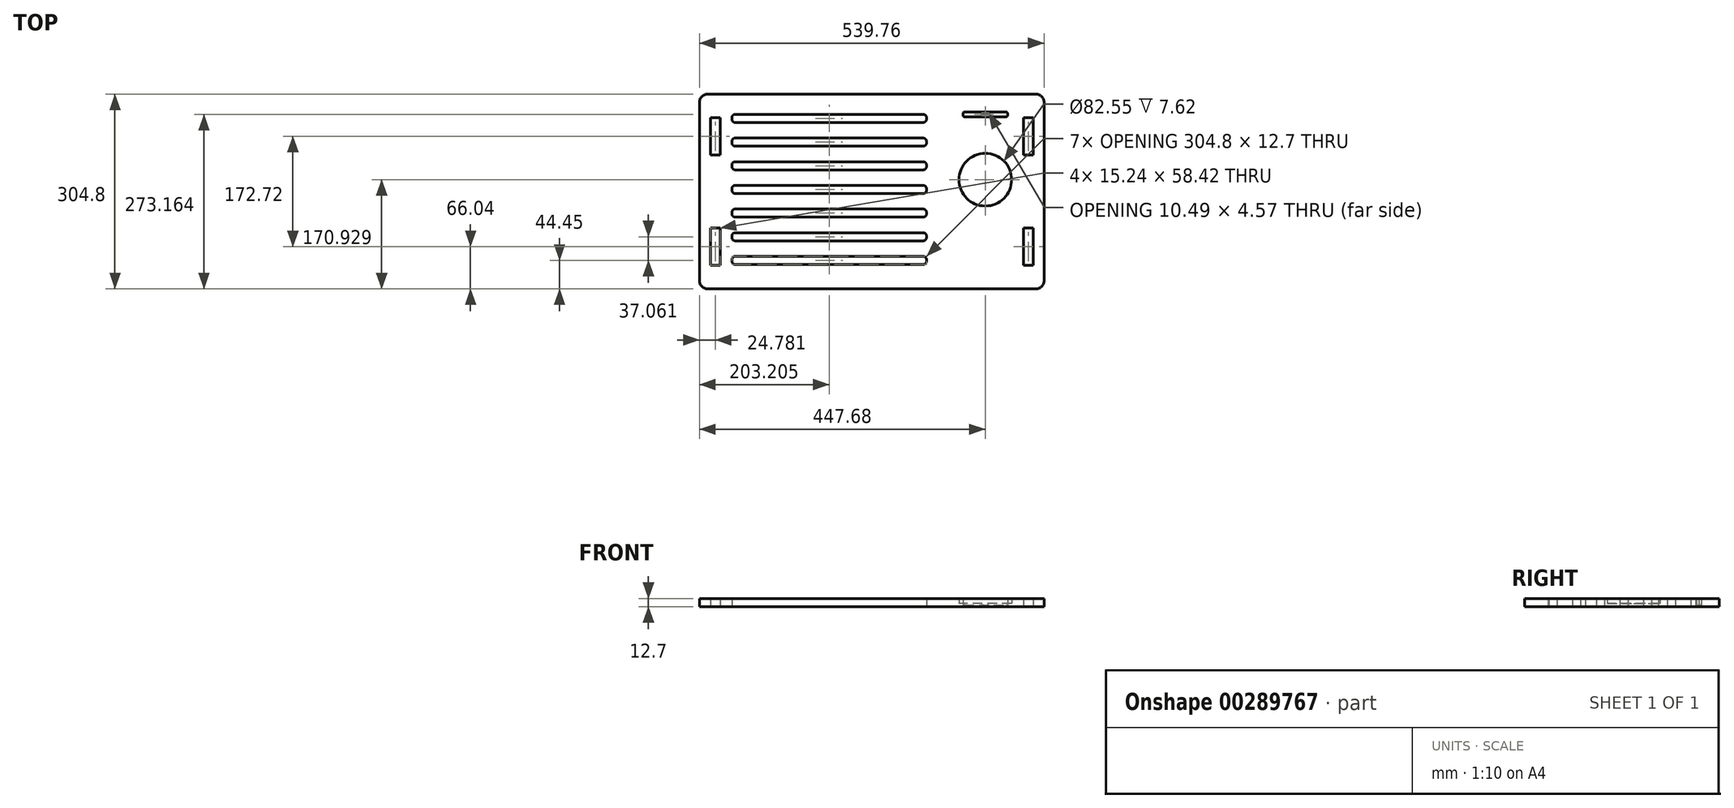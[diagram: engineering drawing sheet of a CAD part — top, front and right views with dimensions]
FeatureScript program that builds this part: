
annotation { "Feature Type Name" : "Feature", "Feature Type Description" : "" }
export const myFeature = defineFeature(function(context is Context, id is Id, definition is map)
    precondition{}
    {
        {
            var Q0;
            Q0=qCreatedBy(makeId("Top.planeOp"),FACE);
            var sketch = newSketch(context, id + "F0", { "sketchPlane" : qUnion([Q0])});
            skLineSegment(sketch, "E0.bottom", {"start": v(269.88, 152.4) * mm, "end": v(-269.88, 152.4) * mm});
            skLineSegment(sketch, "E0.top", {"start": v(269.88, -152.4) * mm, "end": v(-269.88, -152.4) * mm});
            skLineSegment(sketch, "E0.left", {"start": v(269.88, 152.4) * mm, "end": v(269.88, -152.4) * mm});
            skLineSegment(sketch, "E0.right", {"start": v(-269.88, 152.4) * mm, "end": v(-269.88, -152.4) * mm});
            skPoint(sketch, "E0.middle", {"position": v(0, 0) * mm});
            skLineSegment(sketch, "E1.bottom", {"start": v(-219.08, 120.76) * mm, "end": v(85.72, 120.76) * mm});
            skLineSegment(sketch, "E1.top", {"start": v(-219.08, 108.06) * mm, "end": v(85.72, 108.06) * mm});
            skLineSegment(sketch, "E1.left", {"start": v(-219.08, 120.76) * mm, "end": v(-219.08, 108.06) * mm});
            skLineSegment(sketch, "E1.right", {"start": v(85.72, 120.76) * mm, "end": v(85.72, 108.06) * mm});
            skLineSegment(sketch, "E2.bottom", {"start": v(-219.08, 83.7) * mm, "end": v(85.72, 83.7) * mm});
            skLineSegment(sketch, "E2.top", {"start": v(-219.08, 71) * mm, "end": v(85.72, 71) * mm});
            skLineSegment(sketch, "E2.left", {"start": v(-219.08, 83.7) * mm, "end": v(-219.08, 71) * mm});
            skLineSegment(sketch, "E2.right", {"start": v(85.72, 83.7) * mm, "end": v(85.72, 71) * mm});
            skLineSegment(sketch, "E3.bottom", {"start": v(-219.08, -64.54) * mm, "end": v(85.72, -64.54) * mm});
            skLineSegment(sketch, "E3.top", {"start": v(-219.08, -77.24) * mm, "end": v(85.72, -77.24) * mm});
            skLineSegment(sketch, "E3.left", {"start": v(-219.08, -64.54) * mm, "end": v(-219.08, -77.24) * mm});
            skLineSegment(sketch, "E3.right", {"start": v(85.72, -64.54) * mm, "end": v(85.72, -77.24) * mm});
            skLineSegment(sketch, "E4.bottom", {"start": v(-219.08, 9.58) * mm, "end": v(85.72, 9.58) * mm});
            skLineSegment(sketch, "E4.top", {"start": v(-219.08, -3.12) * mm, "end": v(85.72, -3.12) * mm});
            skLineSegment(sketch, "E4.left", {"start": v(-219.08, 9.58) * mm, "end": v(-219.08, -3.12) * mm});
            skLineSegment(sketch, "E4.right", {"start": v(85.72, 9.58) * mm, "end": v(85.72, -3.12) * mm});
            skLineSegment(sketch, "E5.bottom", {"start": v(-219.08, -27.48) * mm, "end": v(85.72, -27.48) * mm});
            skLineSegment(sketch, "E5.top", {"start": v(-219.08, -40.18) * mm, "end": v(85.72, -40.18) * mm});
            skLineSegment(sketch, "E5.left", {"start": v(-219.08, -27.48) * mm, "end": v(-219.08, -40.18) * mm});
            skLineSegment(sketch, "E5.right", {"start": v(85.72, -27.48) * mm, "end": v(85.72, -40.18) * mm});
            skLineSegment(sketch, "E6.bottom", {"start": v(-219.08, 46.64) * mm, "end": v(85.72, 46.64) * mm});
            skLineSegment(sketch, "E6.top", {"start": v(-219.08, 33.94) * mm, "end": v(85.72, 33.94) * mm});
            skLineSegment(sketch, "E6.left", {"start": v(-219.08, 46.64) * mm, "end": v(-219.08, 33.94) * mm});
            skLineSegment(sketch, "E6.right", {"start": v(85.72, 46.64) * mm, "end": v(85.72, 33.94) * mm});
            skLineSegment(sketch, "E7.bottom", {"start": v(-219.08, -101.6) * mm, "end": v(85.72, -101.6) * mm});
            skLineSegment(sketch, "E7.top", {"start": v(-219.08, -114.3) * mm, "end": v(85.72, -114.3) * mm});
            skLineSegment(sketch, "E7.left", {"start": v(-219.08, -101.6) * mm, "end": v(-219.08, -114.3) * mm});
            skLineSegment(sketch, "E7.right", {"start": v(85.72, -101.6) * mm, "end": v(85.72, -114.3) * mm});
            skLineSegment(sketch, "E8", {"start": v(-219.08, 152.4) * mm, "end": v(-219.07, -152.4) * mm, "construction": true});
            skLineSegment(sketch, "E9", {"start": v(-146.4, 71) * mm, "end": v(-146.4, 46.64) * mm, "construction": true});
            skLineSegment(sketch, "E10", {"start": v(-146.45, 108.06) * mm, "end": v(-146.45, 83.7) * mm, "construction": true});
            skLineSegment(sketch, "E11", {"start": v(-146.4, 33.94) * mm, "end": v(-146.4, 9.58) * mm, "construction": true});
            skLineSegment(sketch, "E12", {"start": v(-147.4, -3.12) * mm, "end": v(-147.4, -27.48) * mm, "construction": true});
            skLineSegment(sketch, "E13", {"start": v(-151.42, -40.18) * mm, "end": v(-151.42, -64.54) * mm, "construction": true});
            skLineSegment(sketch, "E14", {"start": v(-148.27, -77.24) * mm, "end": v(-148.27, -101.6) * mm, "construction": true});
            skLineSegment(sketch, "E15", {"start": v(-269.88, 120.76) * mm, "end": v(269.88, 120.76) * mm, "construction": true});
            skLineSegment(sketch, "E16", {"start": v(-269.88, -114.3) * mm, "end": v(269.88, -114.3) * mm, "construction": true});
            skLineSegment(sketch, "E17", {"start": v(-36.06, 137.03) * mm, "end": v(-36.06, 111.63) * mm, "construction": true});
            skLineSegment(sketch, "E18.bottom", {"start": v(142.87, 124.57) * mm, "end": v(212.72, 124.57) * mm});
            skLineSegment(sketch, "E18.top", {"start": v(142.87, 116.95) * mm, "end": v(212.72, 116.95) * mm});
            skLineSegment(sketch, "E18.left", {"start": v(142.87, 124.57) * mm, "end": v(142.87, 116.95) * mm});
            skLineSegment(sketch, "E18.right", {"start": v(212.72, 124.57) * mm, "end": v(212.72, 116.95) * mm});
            skLineSegment(sketch, "E19.bottom", {"start": v(172.55, 123.05) * mm, "end": v(183.05, 123.05) * mm});
            skLineSegment(sketch, "E19.top", {"start": v(172.55, 118.48) * mm, "end": v(183.05, 118.48) * mm});
            skLineSegment(sketch, "E19.left", {"start": v(172.55, 123.05) * mm, "end": v(172.55, 118.48) * mm});
            skLineSegment(sketch, "E19.right", {"start": v(183.05, 123.05) * mm, "end": v(183.05, 118.48) * mm});
            skLineSegment(sketch, "E20", {"start": v(142.87, 120.76) * mm, "end": v(212.72, 120.76) * mm, "construction": true});
            skLineSegment(sketch, "E21", {"start": v(177.8, 116.95) * mm, "end": v(177.8, 124.57) * mm, "construction": true});
            skLineSegment(sketch, "E22", {"start": v(172.55, 120.76) * mm, "end": v(183.05, 120.76) * mm, "construction": true});
            skLineSegment(sketch, "E23", {"start": v(177.8, 118.48) * mm, "end": v(177.8, 123.05) * mm, "construction": true});
            skCircle(sketch, "E24", {"center": v(177.8, 18.53) * mm, "radius": 47.63 * mm});
            skCircle(sketch, "E25", {"center": v(177.8, 18.53) * mm, "radius": 41.28 * mm});
            skLineSegment(sketch, "E26", {"start": v(177.8, 202.35) * mm, "end": v(177.8, -203.89) * mm, "construction": true});
            skLineSegment(sketch, "E27", {"start": v(-245.1, 152.4) * mm, "end": v(-245.1, -152.4) * mm, "construction": true});
            skLineSegment(sketch, "E28.bottom", {"start": v(-237.48, 115.57) * mm, "end": v(-252.72, 115.57) * mm});
            skLineSegment(sketch, "E28.top", {"start": v(-237.48, 57.15) * mm, "end": v(-252.72, 57.15) * mm});
            skLineSegment(sketch, "E28.left", {"start": v(-237.48, 115.57) * mm, "end": v(-237.48, 57.15) * mm});
            skLineSegment(sketch, "E28.right", {"start": v(-252.72, 115.57) * mm, "end": v(-252.72, 57.15) * mm});
            skPoint(sketch, "E28.middle", {"position": v(-245.1, 86.36) * mm});
            skLineSegment(sketch, "E29.MirrorCS", {"start": v(237.48, 115.57) * mm, "end": v(252.72, 115.57) * mm});
            skLineSegment(sketch, "E30.MirrorCS", {"start": v(252.72, 115.57) * mm, "end": v(252.72, 57.15) * mm});
            skLineSegment(sketch, "E31.MirrorCS", {"start": v(237.48, 115.57) * mm, "end": v(237.48, 57.15) * mm});
            skLineSegment(sketch, "E32.MirrorCS", {"start": v(237.48, 57.15) * mm, "end": v(252.72, 57.15) * mm});
            skPoint(sketch, "E33.MirrorP", {"position": v(245.1, 86.36) * mm});
            skLineSegment(sketch, "E34.MirrorCS", {"start": v(-237.48, -115.57) * mm, "end": v(-252.72, -115.57) * mm});
            skLineSegment(sketch, "E35.MirrorCS", {"start": v(-237.48, -57.15) * mm, "end": v(-252.72, -57.15) * mm});
            skPoint(sketch, "E36.MirrorP", {"position": v(-245.1, -86.36) * mm});
            skLineSegment(sketch, "E37.MirrorCS", {"start": v(-237.48, -115.57) * mm, "end": v(-237.48, -57.15) * mm});
            skLineSegment(sketch, "E38.MirrorCS", {"start": v(-252.72, -115.57) * mm, "end": v(-252.72, -57.15) * mm});
            skLineSegment(sketch, "E39.MirrorCS", {"start": v(252.72, -115.57) * mm, "end": v(252.72, -57.15) * mm});
            skLineSegment(sketch, "E40.MirrorCS", {"start": v(237.48, -115.57) * mm, "end": v(237.48, -57.15) * mm});
            skLineSegment(sketch, "E41.MirrorCS", {"start": v(237.48, -115.57) * mm, "end": v(252.72, -115.57) * mm});
            skPoint(sketch, "E42.MirrorP", {"position": v(245.1, -86.36) * mm});
            skLineSegment(sketch, "E43.MirrorCS", {"start": v(237.48, -57.15) * mm, "end": v(252.72, -57.15) * mm});
            skLineSegment(sketch, "E44.MirrorCS", {"start": v(269.88, -152.4) * mm, "end": v(269.88, 152.4) * mm});
            skSolve(sketch);
        }
        {
            var Q0;
            Q0=makeQuery(id+"F0.imprint","IMPRINT",FACE,{"disambiguationData":[TD([[makeQuery(id+"F0.imprint","IMPRINT",EDGE,{"derivedFrom":sQuery(id+"F0.wireOp",EDGE,"E0.bottom")}),1.0]])]});
            extrude(context, id + "F1", {"entities" : qUnion([Q0]), "depth" : 12.7 * mm});
        }
        {
            var Q0;
            Q0=makeQuery(id+"F0.imprint","IMPRINT",FACE,{"disambiguationData":[TD([[makeQuery(id+"F0.imprint","IMPRINT",EDGE,{"derivedFrom":sQuery(id+"F0.wireOp",EDGE,"E18.bottom")}),-1.0]])]});
            extrude(context, id + "F2", {"entities" : qUnion([Q0]), "operationType" : NewBodyOperationType.ADD, "depth" : 2.54 * mm});
        }
        {
            var Q0;
            Q0=makeQuery(id+"F0.imprint","IMPRINT",FACE,{"disambiguationData":[TD([[makeQuery(id+"F0.imprint","IMPRINT",EDGE,{"derivedFrom":sQuery(id+"F0.wireOp",EDGE,"E24")}),1.0]])]});
            extrude(context, id + "F3", {"entities" : qUnion([Q0]), "operationType" : NewBodyOperationType.ADD, "depth" : 12.7 * mm});
        }
        {
            var Q0;
            Q0=makeQuery(id+"F0.imprint","IMPRINT",FACE,{"disambiguationData":[TD([[makeQuery(id+"F0.imprint","IMPRINT",EDGE,{"derivedFrom":sQuery(id+"F0.wireOp",EDGE,"E25")}),1.0]])]});
            extrude(context, id + "F4", {"entities" : qUnion([Q0]), "operationType" : NewBodyOperationType.ADD, "depth" : 5.08 * mm});
        }
        {
            var Q0;
            Q0=makeQuery(id+"F1.opExtrude","SWEPT_EDGE",EDGE,{"disambiguationData":[OSD([sQuery(id+"F0.wireOp",EDGE,"E0.bottom"),sQuery(id+"F0.wireOp",EDGE,"E0.right")])]});
            var Q1;
            Q1=makeQuery(id+"F1.opExtrude","SWEPT_EDGE",EDGE,{"disambiguationData":[OSD([sQuery(id+"F0.wireOp",EDGE,"E0.bottom"),sQuery(id+"F0.wireOp",EDGE,"E0.left")])]});
            var Q2;
            Q2=makeQuery(id+"F1.opExtrude","SWEPT_EDGE",EDGE,{"disambiguationData":[OSD([sQuery(id+"F0.wireOp",EDGE,"E0.top"),sQuery(id+"F0.wireOp",EDGE,"E0.left")])]});
            var Q3;
            Q3=makeQuery(id+"F1.opExtrude","SWEPT_EDGE",EDGE,{"disambiguationData":[OSD([sQuery(id+"F0.wireOp",EDGE,"E0.top"),sQuery(id+"F0.wireOp",EDGE,"E0.right")])]});
            fillet(context, id + "F5", {"entities" : qUnion([Q0, Q1, Q2, Q3]), "radius" : 12.7 * mm, "tangentPropagation" : true, "allowEdgeOverflow" : false});
        }
        {
            var Q0;
            Q0=makeQuery(id+"F1.opExtrude","SWEPT_EDGE",EDGE,{"disambiguationData":[OSD([sQuery(id+"F0.wireOp",EDGE,"E1.bottom"),sQuery(id+"F0.wireOp",EDGE,"E1.left")])]});
            var Q1;
            Q1=makeQuery(id+"F1.opExtrude","SWEPT_EDGE",EDGE,{"disambiguationData":[OSD([sQuery(id+"F0.wireOp",EDGE,"E1.bottom"),sQuery(id+"F0.wireOp",EDGE,"E1.right")])]});
            var Q2;
            Q2=makeQuery(id+"F1.opExtrude","SWEPT_EDGE",EDGE,{"disambiguationData":[OSD([sQuery(id+"F0.wireOp",EDGE,"E6.top"),sQuery(id+"F0.wireOp",EDGE,"E6.left")])]});
            var Q3;
            Q3=makeQuery(id+"F1.opExtrude","SWEPT_EDGE",EDGE,{"disambiguationData":[OSD([sQuery(id+"F0.wireOp",EDGE,"E4.top"),sQuery(id+"F0.wireOp",EDGE,"E4.left")])]});
            var Q4;
            Q4=makeQuery(id+"F1.opExtrude","SWEPT_EDGE",EDGE,{"disambiguationData":[OSD([sQuery(id+"F0.wireOp",EDGE,"E5.top"),sQuery(id+"F0.wireOp",EDGE,"E5.left")])]});
            var Q5;
            Q5=makeQuery(id+"F1.opExtrude","SWEPT_EDGE",EDGE,{"disambiguationData":[OSD([sQuery(id+"F0.wireOp",EDGE,"E3.top"),sQuery(id+"F0.wireOp",EDGE,"E3.left")])]});
            var Q6;
            Q6=makeQuery(id+"F1.opExtrude","SWEPT_EDGE",EDGE,{"disambiguationData":[OSD([sQuery(id+"F0.wireOp",EDGE,"E7.top"),sQuery(id+"F0.wireOp",EDGE,"E7.left")])]});
            var Q7;
            Q7=makeQuery(id+"F1.opExtrude","SWEPT_EDGE",EDGE,{"disambiguationData":[OSD([sQuery(id+"F0.wireOp",EDGE,"E1.top"),sQuery(id+"F0.wireOp",EDGE,"E1.left")])]});
            var Q8;
            Q8=makeQuery(id+"F1.opExtrude","SWEPT_EDGE",EDGE,{"disambiguationData":[OSD([sQuery(id+"F0.wireOp",EDGE,"E2.top"),sQuery(id+"F0.wireOp",EDGE,"E2.left")])]});
            var Q9;
            Q9=makeQuery(id+"F1.opExtrude","SWEPT_EDGE",EDGE,{"disambiguationData":[OSD([sQuery(id+"F0.wireOp",EDGE,"E1.top"),sQuery(id+"F0.wireOp",EDGE,"E1.right")])]});
            var Q10;
            Q10=makeQuery(id+"F1.opExtrude","SWEPT_EDGE",EDGE,{"disambiguationData":[OSD([sQuery(id+"F0.wireOp",EDGE,"E2.top"),sQuery(id+"F0.wireOp",EDGE,"E2.right")])]});
            var Q11;
            Q11=makeQuery(id+"F1.opExtrude","SWEPT_EDGE",EDGE,{"disambiguationData":[OSD([sQuery(id+"F0.wireOp",EDGE,"E6.top"),sQuery(id+"F0.wireOp",EDGE,"E6.right")])]});
            var Q12;
            Q12=makeQuery(id+"F1.opExtrude","SWEPT_EDGE",EDGE,{"disambiguationData":[OSD([sQuery(id+"F0.wireOp",EDGE,"E4.top"),sQuery(id+"F0.wireOp",EDGE,"E4.right")])]});
            var Q13;
            Q13=makeQuery(id+"F1.opExtrude","SWEPT_EDGE",EDGE,{"disambiguationData":[OSD([sQuery(id+"F0.wireOp",EDGE,"E5.top"),sQuery(id+"F0.wireOp",EDGE,"E5.right")])]});
            var Q14;
            Q14=makeQuery(id+"F1.opExtrude","SWEPT_EDGE",EDGE,{"disambiguationData":[OSD([sQuery(id+"F0.wireOp",EDGE,"E3.top"),sQuery(id+"F0.wireOp",EDGE,"E3.right")])]});
            var Q15;
            Q15=makeQuery(id+"F1.opExtrude","SWEPT_EDGE",EDGE,{"disambiguationData":[OSD([sQuery(id+"F0.wireOp",EDGE,"E7.top"),sQuery(id+"F0.wireOp",EDGE,"E7.right")])]});
            var Q16;
            Q16=makeQuery(id+"F1.opExtrude","SWEPT_EDGE",EDGE,{"disambiguationData":[OSD([sQuery(id+"F0.wireOp",EDGE,"E7.bottom"),sQuery(id+"F0.wireOp",EDGE,"E7.right")])]});
            var Q17;
            Q17=makeQuery(id+"F1.opExtrude","SWEPT_EDGE",EDGE,{"disambiguationData":[OSD([sQuery(id+"F0.wireOp",EDGE,"E3.bottom"),sQuery(id+"F0.wireOp",EDGE,"E3.right")])]});
            var Q18;
            Q18=makeQuery(id+"F1.opExtrude","SWEPT_EDGE",EDGE,{"disambiguationData":[OSD([sQuery(id+"F0.wireOp",EDGE,"E5.bottom"),sQuery(id+"F0.wireOp",EDGE,"E5.right")])]});
            var Q19;
            Q19=makeQuery(id+"F1.opExtrude","SWEPT_EDGE",EDGE,{"disambiguationData":[OSD([sQuery(id+"F0.wireOp",EDGE,"E4.bottom"),sQuery(id+"F0.wireOp",EDGE,"E4.right")])]});
            var Q20;
            Q20=makeQuery(id+"F1.opExtrude","SWEPT_EDGE",EDGE,{"disambiguationData":[OSD([sQuery(id+"F0.wireOp",EDGE,"E6.bottom"),sQuery(id+"F0.wireOp",EDGE,"E6.right")])]});
            var Q21;
            Q21=makeQuery(id+"F1.opExtrude","SWEPT_EDGE",EDGE,{"disambiguationData":[OSD([sQuery(id+"F0.wireOp",EDGE,"E2.bottom"),sQuery(id+"F0.wireOp",EDGE,"E2.right")])]});
            var Q22;
            Q22=makeQuery(id+"F1.opExtrude","SWEPT_EDGE",EDGE,{"disambiguationData":[OSD([sQuery(id+"F0.wireOp",EDGE,"E7.bottom"),sQuery(id+"F0.wireOp",EDGE,"E7.left")])]});
            var Q23;
            Q23=makeQuery(id+"F1.opExtrude","SWEPT_EDGE",EDGE,{"disambiguationData":[OSD([sQuery(id+"F0.wireOp",EDGE,"E3.bottom"),sQuery(id+"F0.wireOp",EDGE,"E3.left")])]});
            var Q24;
            Q24=makeQuery(id+"F1.opExtrude","SWEPT_EDGE",EDGE,{"disambiguationData":[OSD([sQuery(id+"F0.wireOp",EDGE,"E5.bottom"),sQuery(id+"F0.wireOp",EDGE,"E5.left")])]});
            var Q25;
            Q25=makeQuery(id+"F1.opExtrude","SWEPT_EDGE",EDGE,{"disambiguationData":[OSD([sQuery(id+"F0.wireOp",EDGE,"E4.bottom"),sQuery(id+"F0.wireOp",EDGE,"E4.left")])]});
            var Q26;
            Q26=makeQuery(id+"F1.opExtrude","SWEPT_EDGE",EDGE,{"disambiguationData":[OSD([sQuery(id+"F0.wireOp",EDGE,"E6.bottom"),sQuery(id+"F0.wireOp",EDGE,"E6.left")])]});
            var Q27;
            Q27=makeQuery(id+"F1.opExtrude","SWEPT_EDGE",EDGE,{"disambiguationData":[OSD([sQuery(id+"F0.wireOp",EDGE,"E2.bottom"),sQuery(id+"F0.wireOp",EDGE,"E2.left")])]});
            fillet(context, id + "F6", {"entities" : qUnion([Q0, Q1, Q2, Q3, Q4, Q5, Q6, Q7, Q8, Q9, Q10, Q11, Q12, Q13, Q14, Q15, Q16, Q17, Q18, Q19, Q20, Q21, Q22, Q23, Q24, Q25, Q26, Q27]), "radius" : 5.08 * mm, "tangentPropagation" : true, "allowEdgeOverflow" : false});
        }
        {
            var Q0;
            Q0=makeQuery(id+"F1.opExtrude","SWEPT_EDGE",EDGE,{"disambiguationData":[OSD([sQuery(id+"F0.wireOp",EDGE,"E18.bottom"),sQuery(id+"F0.wireOp",EDGE,"E18.left")])]});
            var Q1;
            Q1=makeQuery(id+"F1.opExtrude","SWEPT_EDGE",EDGE,{"disambiguationData":[OSD([sQuery(id+"F0.wireOp",EDGE,"E18.bottom"),sQuery(id+"F0.wireOp",EDGE,"E18.right")])]});
            var Q2;
            Q2=makeQuery(id+"F1.opExtrude","SWEPT_EDGE",EDGE,{"disambiguationData":[OSD([sQuery(id+"F0.wireOp",EDGE,"E18.top"),sQuery(id+"F0.wireOp",EDGE,"E18.left")])]});
            var Q3;
            Q3=makeQuery(id+"F1.opExtrude","SWEPT_EDGE",EDGE,{"disambiguationData":[OSD([sQuery(id+"F0.wireOp",EDGE,"E18.top"),sQuery(id+"F0.wireOp",EDGE,"E18.right")])]});
            fillet(context, id + "F7", {"entities" : qUnion([Q0, Q1, Q2, Q3]), "radius" : 2.54 * mm, "tangentPropagation" : true, "allowEdgeOverflow" : false});
        }
        {
            var Q0;
            Q0=makeQuery(id+"F2.opExtrude","SWEPT_EDGE",EDGE,{"disambiguationData":[OSD([sQuery(id+"F0.wireOp",EDGE,"E19.bottom"),sQuery(id+"F0.wireOp",EDGE,"E19.left")])]});
            var Q1;
            Q1=makeQuery(id+"F2.opExtrude","SWEPT_EDGE",EDGE,{"disambiguationData":[OSD([sQuery(id+"F0.wireOp",EDGE,"E19.bottom"),sQuery(id+"F0.wireOp",EDGE,"E19.right")])]});
            var Q2;
            Q2=makeQuery(id+"F2.opExtrude","SWEPT_EDGE",EDGE,{"disambiguationData":[OSD([sQuery(id+"F0.wireOp",EDGE,"E19.top"),sQuery(id+"F0.wireOp",EDGE,"E19.right")])]});
            var Q3;
            Q3=makeQuery(id+"F2.opExtrude","SWEPT_EDGE",EDGE,{"disambiguationData":[OSD([sQuery(id+"F0.wireOp",EDGE,"E19.top"),sQuery(id+"F0.wireOp",EDGE,"E19.left")])]});
            fillet(context, id + "F8", {"entities" : qUnion([Q0, Q1, Q2, Q3]), "radius" : 2.03 * mm, "tangentPropagation" : true, "allowEdgeOverflow" : false});
        }
    });
